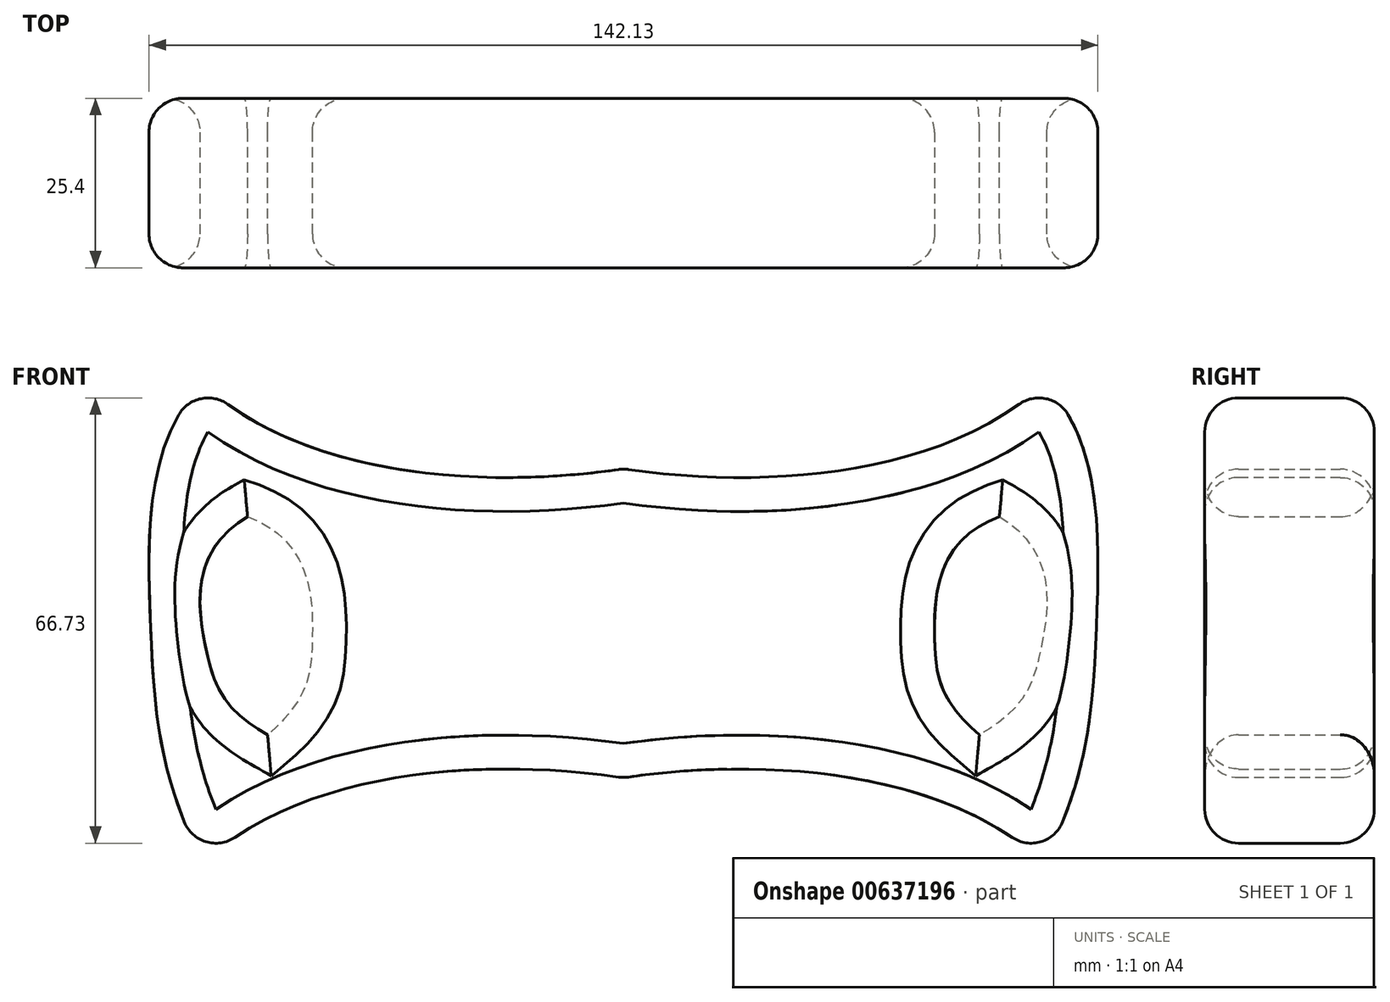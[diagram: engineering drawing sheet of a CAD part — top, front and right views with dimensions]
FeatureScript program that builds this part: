
annotation { "Feature Type Name" : "Feature", "Feature Type Description" : "" }
export const myFeature = defineFeature(function(context is Context, id is Id, definition is map)
    precondition{}
    {
        {
            var Q0;
            Q0=qCreatedBy(makeId("Front.planeOp"),FACE);
            var sketch = newSketch(context, id + "F0", { "sketchPlane" : qUnion([Q0])});
            skFitSpline(sketch, "E0", {"points": [v(-68.77, 16.07) * mm, v(-5.8, 3.34) * mm], "startDerivative": vector(42.93, -40.36) * mm, "endDerivative": vector(66.73, 10.01) * mm});
            skFitSpline(sketch, "E1.MirrorCS", {"points": [v(-68.77, -55.7) * mm, v(-5.8, -42.97) * mm], "startDerivative": vector(42.93, 40.36) * mm, "endDerivative": vector(66.73, -10.01) * mm});
            skFitSpline(sketch, "E2", {"points": [v(-68.77, 16.07) * mm, v(-76.65, -19.82) * mm, v(-68.77, -55.7) * mm], "startDerivative": vector(-52.69, -50.24) * mm, "endDerivative": vector(40.68, -79.41) * mm});
            skFitSpline(sketch, "E3.MirrorCS", {"points": [v(57.18, 16.07) * mm, v(-5.8, 3.34) * mm], "startDerivative": vector(-42.93, -40.36) * mm, "endDerivative": vector(-66.73, 10.01) * mm});
            skFitSpline(sketch, "E4.MirrorCS", {"points": [v(57.18, 16.07) * mm, v(65.05, -19.82) * mm, v(57.18, -55.7) * mm], "startDerivative": vector(52.69, -50.24) * mm, "endDerivative": vector(-40.68, -79.41) * mm});
            skFitSpline(sketch, "E5.MirrorCS", {"points": [v(57.18, -55.7) * mm, v(-5.8, -42.97) * mm], "startDerivative": vector(-42.93, 40.36) * mm, "endDerivative": vector(-66.73, -10.01) * mm});
            skFitSpline(sketch, "E6", {"points": [v(-62.1, -3.86) * mm, v(-68.33, -23.55) * mm, v(-59.11, -36.52) * mm], "startDerivative": vector(-48.96, -28.56) * mm, "endDerivative": vector(44.23, -25.27) * mm});
            skLineSegment(sketch, "E7", {"start": v(-62.1, -3.86) * mm, "end": v(-62.1, -3.86) * mm});
            skFitSpline(sketch, "E8.MirrorCS", {"points": [v(-62.1, -3.86) * mm, v(-52.4, -22.1) * mm, v(-59.11, -36.52) * mm], "startDerivative": vector(53.33, -19.19) * mm, "endDerivative": vector(-38.9, -32.89) * mm});
            skFitSpline(sketch, "E9.MirrorCS", {"points": [v(50.51, -3.86) * mm, v(56.74, -23.55) * mm, v(47.52, -36.52) * mm], "startDerivative": vector(48.96, -28.56) * mm, "endDerivative": vector(-44.23, -25.27) * mm});
            skFitSpline(sketch, "E10.MirrorCS", {"points": [v(50.51, -3.86) * mm, v(40.8, -22.1) * mm, v(47.52, -36.52) * mm], "startDerivative": vector(-53.33, -19.19) * mm, "endDerivative": vector(38.9, -32.89) * mm});
            skSolve(sketch);
        }
        {
            var Q0;
            Q0 = qSketchRegion(id + "F0", true);
            extrude(context, id + "F1", {"entities" : qUnion([Q0]), "depth" : 25.4 * mm, "offsetDistance" : 25.4 * mm});
        }
        {
            var Q0;
            Q0=makeQuery(id+"F1.opExtrude","CAP_FACE",FACE,{"disambiguationData":[OSD([sQuery(id+"F0.wireOp",EDGE,"E0"),sQuery(id+"F0.wireOp",EDGE,"E1.MirrorCS"),sQuery(id+"F0.wireOp",EDGE,"E2"),sQuery(id+"F0.wireOp",EDGE,"E3.MirrorCS"),sQuery(id+"F0.wireOp",EDGE,"E4.MirrorCS"),sQuery(id+"F0.wireOp",EDGE,"E5.MirrorCS")])],"isStart":false});
            var Q1;
            Q1=makeQuery(id+"F1.opExtrude","SWEPT_FACE",FACE,{"disambiguationData":[OSD([sQuery(id+"F0.wireOp",EDGE,"E1.MirrorCS")])]});
            var Q2;
            Q2=makeQuery(id+"F1.opExtrude","SWEPT_FACE",FACE,{"disambiguationData":[OSD([sQuery(id+"F0.wireOp",EDGE,"E5.MirrorCS")])]});
            var Q3;
            Q3=makeQuery(id+"F1.opExtrude","SWEPT_FACE",FACE,{"disambiguationData":[OSD([sQuery(id+"F0.wireOp",EDGE,"E2")])]});
            var Q4;
            Q4=makeQuery(id+"F1.opExtrude","SWEPT_FACE",FACE,{"disambiguationData":[OSD([sQuery(id+"F0.wireOp",EDGE,"E0")])]});
            var Q5;
            Q5=makeQuery(id+"F1.opExtrude","SWEPT_FACE",FACE,{"disambiguationData":[OSD([sQuery(id+"F0.wireOp",EDGE,"E3.MirrorCS")])]});
            var Q6;
            Q6=makeQuery(id+"F1.opExtrude","SWEPT_FACE",FACE,{"disambiguationData":[OSD([sQuery(id+"F0.wireOp",EDGE,"E4.MirrorCS")])]});
            var Q7;
            Q7=makeQuery(id+"F1.opExtrude","CAP_FACE",FACE,{"disambiguationData":[OSD([sQuery(id+"F0.wireOp",EDGE,"E0"),sQuery(id+"F0.wireOp",EDGE,"E1.MirrorCS"),sQuery(id+"F0.wireOp",EDGE,"E2"),sQuery(id+"F0.wireOp",EDGE,"E3.MirrorCS"),sQuery(id+"F0.wireOp",EDGE,"E4.MirrorCS"),sQuery(id+"F0.wireOp",EDGE,"E5.MirrorCS")])],"isStart":true});
            fillet(context, id + "F2", {"entities" : qUnion([Q0, Q1, Q2, Q3, Q4, Q5, Q6, Q7]), "radius" : 5.08 * mm, "tangentPropagation" : true, "allowEdgeOverflow" : false});
        }
    });
